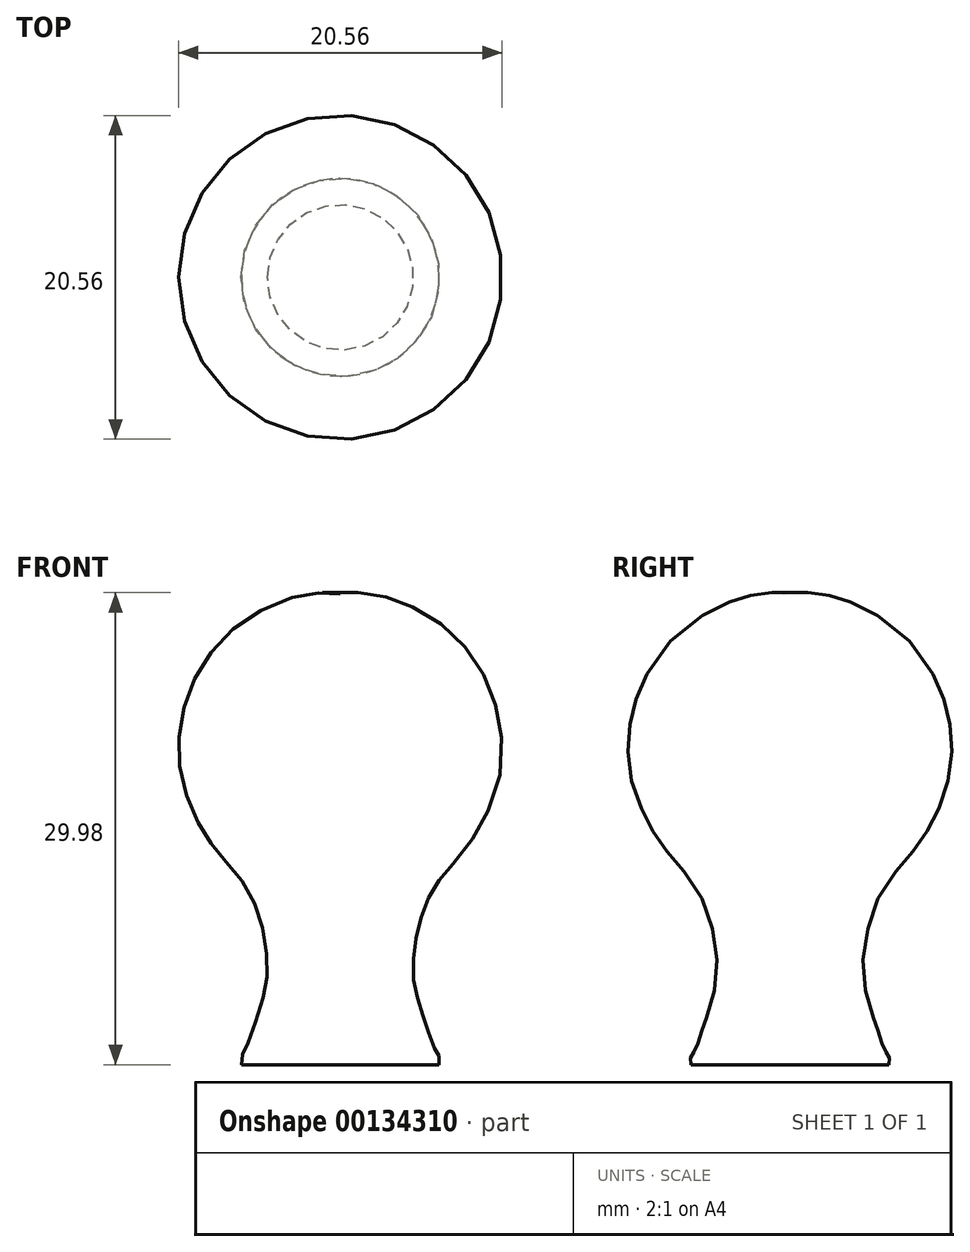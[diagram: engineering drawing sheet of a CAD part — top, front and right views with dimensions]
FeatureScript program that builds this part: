
annotation { "Feature Type Name" : "Feature", "Feature Type Description" : "" }
export const myFeature = defineFeature(function(context is Context, id is Id, definition is map)
    precondition{}
    {
        {
            var Q0;
            Q0=qCreatedBy(makeId("Front.planeOp"),FACE);
            var sketch = newSketch(context, id + "F0", { "sketchPlane" : qUnion([Q0])});
            skLineSegment(sketch, "E0", {"start": v(-6.27, 0) * mm, "end": v(6.08, 0) * mm});
            skLineSegment(sketch, "E1", {"start": v(0, 29.9) * mm, "end": v(0, 0) * mm});
            skFitSpline(sketch, "E2", {"points": [v(0, 29.9) * mm, v(-2.09, 29.9) * mm, v(-6, 28.26) * mm, v(-8.84, 25.25) * mm, v(-10.13, 21.73) * mm, v(-10.09, 18.2) * mm, v(-8.8, 14.98) * mm, v(-7.46, 13.13) * mm, v(-5.87, 11.1) * mm, v(-4.93, 8.57) * mm, v(-4.63, 6) * mm, v(-4.93, 4.18) * mm, v(-5.7, 1.82) * mm, v(-6.09, 0.83) * mm, v(-6.28, 0.54) * mm, v(-6.27, 0) * mm], "startDerivative": vector(-30.27, 3.24) * mm, "endDerivative": vector(2.58, -18.86) * mm});
            skFitSpline(sketch, "E3.MirrorCS", {"points": [v(0, 29.9) * mm, v(2.09, 29.9) * mm, v(6, 28.26) * mm, v(8.84, 25.25) * mm, v(10.13, 21.73) * mm, v(10.09, 18.2) * mm, v(8.8, 14.98) * mm, v(7.46, 13.13) * mm, v(5.87, 11.1) * mm, v(4.93, 8.57) * mm, v(4.63, 6) * mm, v(4.93, 4.18) * mm, v(5.7, 1.82) * mm, v(6.09, 0.83) * mm, v(6.28, 0.54) * mm, v(6.27, 0) * mm], "startDerivative": vector(30.27, 3.24) * mm, "endDerivative": vector(-2.58, -18.86) * mm});
            skSolve(sketch);
        }
        {
            var Q0;
            {var subQ2=sQuery(id+"F0.wireOp",EDGE,"E1");Q0=makeQuery(id+"F0.imprint","IMPRINT",FACE,{"disambiguationData":[TD([[makeQuery(id+"F0.imprint","IMPRINT",EDGE,{"derivedFrom":subQ2}),-1.0]])]});}
            var Q1;
            Q1=sQuery(id+"F0.wireOp",EDGE,"E1");
            revolve(context, id + "F1", {"entities" : qUnion([Q0]), "axis" : qUnion([Q1]), "revolveType" : RevolveType.FULL});
        }
    });
